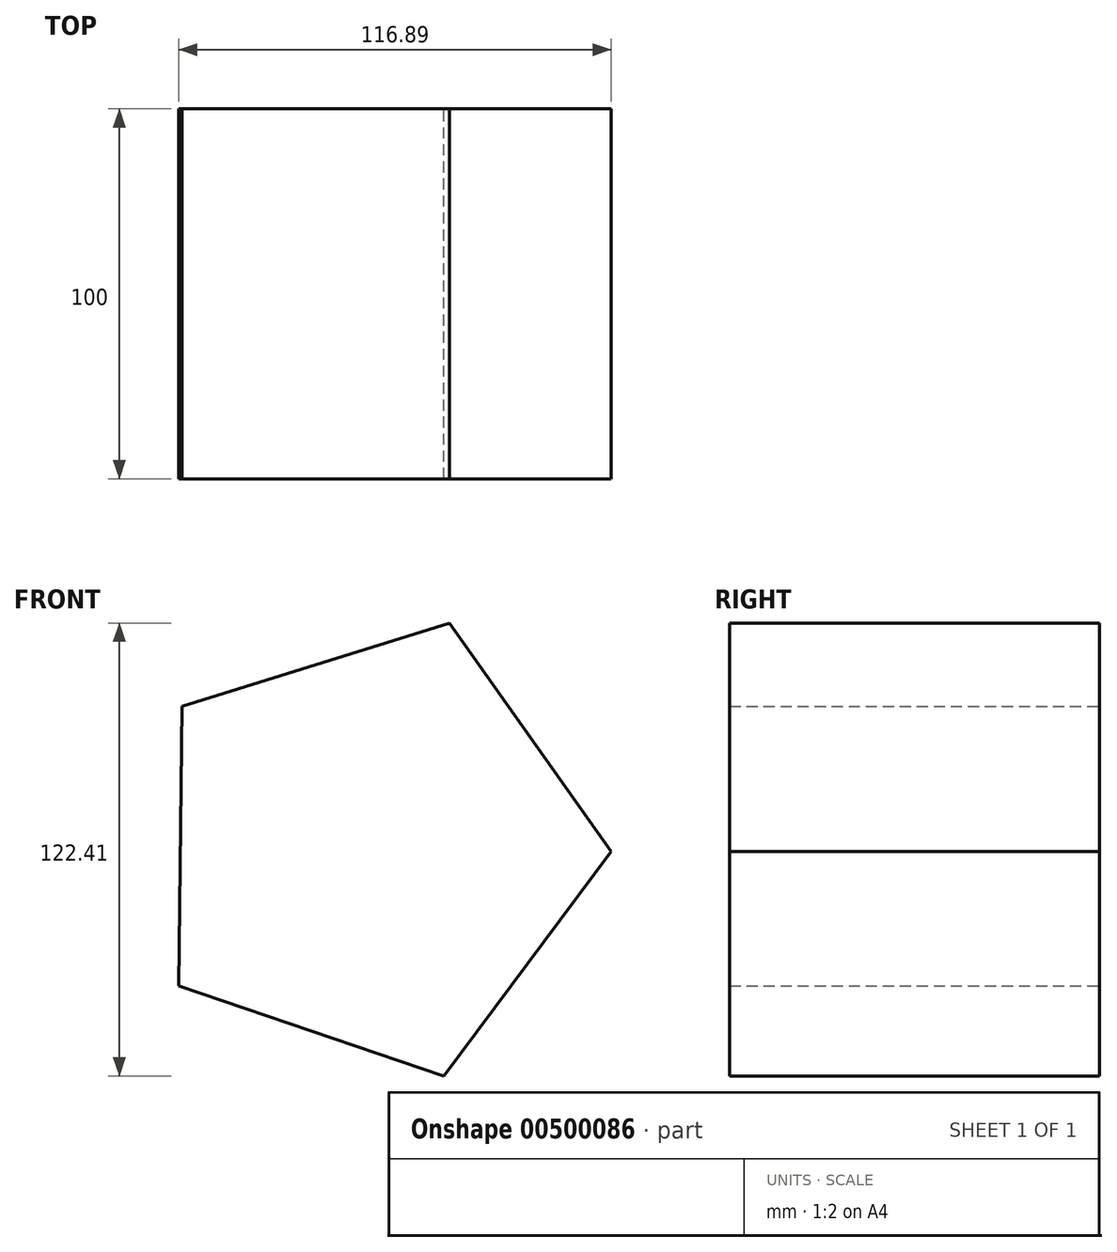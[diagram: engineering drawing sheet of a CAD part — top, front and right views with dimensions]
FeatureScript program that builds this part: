
annotation { "Feature Type Name" : "Feature", "Feature Type Description" : "" }
export const myFeature = defineFeature(function(context is Context, id is Id, definition is map)
    precondition{}
    {
        {
            var Q0;
            Q0=qCreatedBy(makeId("Front.planeOp"),FACE);
            var sketch = newSketch(context, id + "F0", { "sketchPlane" : qUnion([Q0])});
            skCircle(sketch, "E0.cCircle", {"center": v(24.78, -34.25) * mm, "radius": 64.36 * mm, "construction": true});
            skLineSegment(sketch, "E0.0", {"start": v(-26.82, 4.23) * mm, "end": v(45.42, 26.7) * mm});
            skLineSegment(sketch, "E0.1", {"start": v(45.42, 26.7) * mm, "end": v(89.13, -35.05) * mm});
            skLineSegment(sketch, "E0.2", {"start": v(89.13, -35.05) * mm, "end": v(43.9, -95.7) * mm});
            skLineSegment(sketch, "E0.3", {"start": v(43.9, -95.7) * mm, "end": v(-27.76, -71.43) * mm});
            skLineSegment(sketch, "E0.4", {"start": v(-27.76, -71.43) * mm, "end": v(-26.82, 4.23) * mm});
            skSolve(sketch);
        }
        {
            var Q0;
            Q0=makeQuery(id+"F0.imprint","IMPRINT",FACE,{"disambiguationData":[TD([[makeQuery(id+"F0.imprint","IMPRINT",EDGE,{"derivedFrom":sQuery(id+"F0.wireOp",EDGE,"E0.0")}),-1.0]])]});
            extrude(context, id + "F1", {"entities" : qUnion([Q0]), "endBound" : BoundingType.SYMMETRIC, "depth" : 100 * mm});
        }
    });
